annotation { "Feature Type Name" : "Feature", "Feature Type Description" : "" }
export const myFeature = defineFeature(function(context is Context, id is Id, definition is map)
    precondition{}
    {
        {
            var Q0;
            Q0=qCreatedBy(makeId("Front.planeOp"),FACE);
            var sketch = newSketch(context, id + "F0", { "sketchPlane" : qUnion([Q0])});
            skLineSegment(sketch, "E0.bottom", {"start": v(34.93, 57.15) * mm, "end": v(-34.93, 57.15) * mm});
            skLineSegment(sketch, "E0.top", {"start": v(34.93, -57.15) * mm, "end": v(-34.93, -57.15) * mm});
            skLineSegment(sketch, "E0.left", {"start": v(34.93, 57.15) * mm, "end": v(34.93, -57.15) * mm});
            skLineSegment(sketch, "E0.right", {"start": v(-34.93, 57.15) * mm, "end": v(-34.93, -57.15) * mm});
            skPoint(sketch, "E0.middle", {"position": v(0, 0) * mm});
            skLineSegment(sketch, "E1.bottom", {"start": v(4.76, 12.7) * mm, "end": v(-4.76, 12.7) * mm});
            skLineSegment(sketch, "E1.top", {"start": v(4.76, -12.7) * mm, "end": v(-4.76, -12.7) * mm});
            skLineSegment(sketch, "E1.left", {"start": v(4.76, 12.7) * mm, "end": v(4.76, -12.7) * mm});
            skLineSegment(sketch, "E1.right", {"start": v(-4.76, 12.7) * mm, "end": v(-4.76, -12.7) * mm});
            skCircle(sketch, "E2", {"center": v(0, 26.5) * mm, "radius": 1.9 * mm});
            skCircle(sketch, "E3", {"center": v(0, -31.92) * mm, "radius": 1.9 * mm});
            skText(sketch, "E4", { "text": "Bright Ideas", "fontName": "OpenSans-Regular.ttf"});
            skPoint(sketch, "E5", {"position": v(0, 57.15) * mm});
            const initialGuessF0  = {"E4": [-0.0345, 0.03762, 1, 0, 0.00889]};
            skSetInitialGuess(sketch, initialGuessF0);
            skSolve(sketch);
        }
        {
            var Q0;
            Q0 = qSketchRegion(id + "F0", true);
            extrude(context, id + "F1", {"entities" : qUnion([Q0]), "depth" : 5.08 * mm});
        }
    });